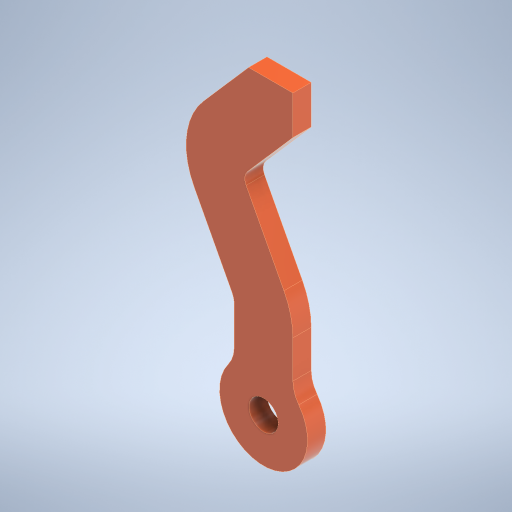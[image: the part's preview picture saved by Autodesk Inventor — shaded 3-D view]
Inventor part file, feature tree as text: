
AUTODESK INVENTOR PART (.ipt)
format: ipt  version: 2023.2 (Build 272271000, 271)  size: 272,896 bytes
history: native  units: mm
features: other x3, sketch x2, extrude x1
ambient origin geometry x8: Origin, YZ Plane, XZ Plane, XY Plane, X Axis, Y Axis, Z Axis, Center Point
bodies: Solid1 (feature_tree)
feature tree (6):
  other  "gripper.ipt"
  extrude  "Extrusion1"  Depth=4.0mm
  other  "Solid1::gripper.ipt"
  other  "TaggingFeature1"
  sketch  "Sketch1"  dims[d0=10.0mm d1=4.0mm]
  sketch  "Sketch2"  dims[d2=10.0mm d3=0.0mm]
